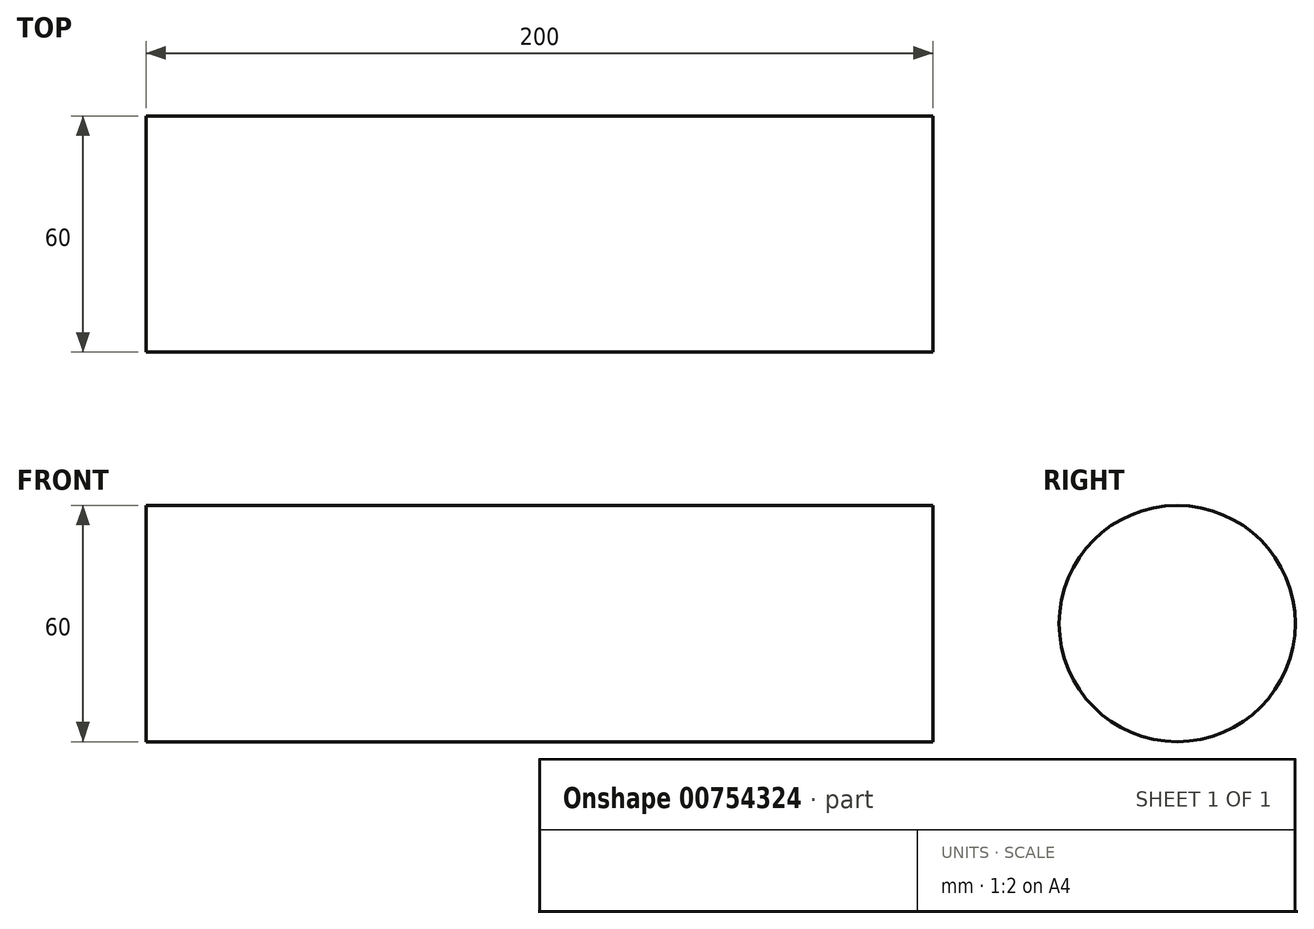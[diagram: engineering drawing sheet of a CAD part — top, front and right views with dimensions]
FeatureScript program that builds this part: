
annotation { "Feature Type Name" : "Feature", "Feature Type Description" : "" }
export const myFeature = defineFeature(function(context is Context, id is Id, definition is map)
    precondition{}
    {
        {
            var Q0;
            Q0=qCreatedBy(makeId("Right.planeOp"),FACE);
            var sketch = newSketch(context, id + "F0", { "sketchPlane" : qUnion([Q0])});
            skCircle(sketch, "E0", {"center": v(0, 0) * mm, "radius": 30 * mm});
            skSolve(sketch);
        }
        {
            var Q0;
            Q0=makeQuery(id+"F0.imprint","IMPRINT",FACE,{"disambiguationData":[TD([[makeQuery(id+"F0.imprint","IMPRINT",EDGE,{"derivedFrom":sQuery(id+"F0.wireOp",EDGE,"E0")}),1.0]])]});
            extrude(context, id + "F1", {"entities" : qUnion([Q0]), "depth" : 200 * mm, "offsetDistance" : 25 * mm});
        }
    });
